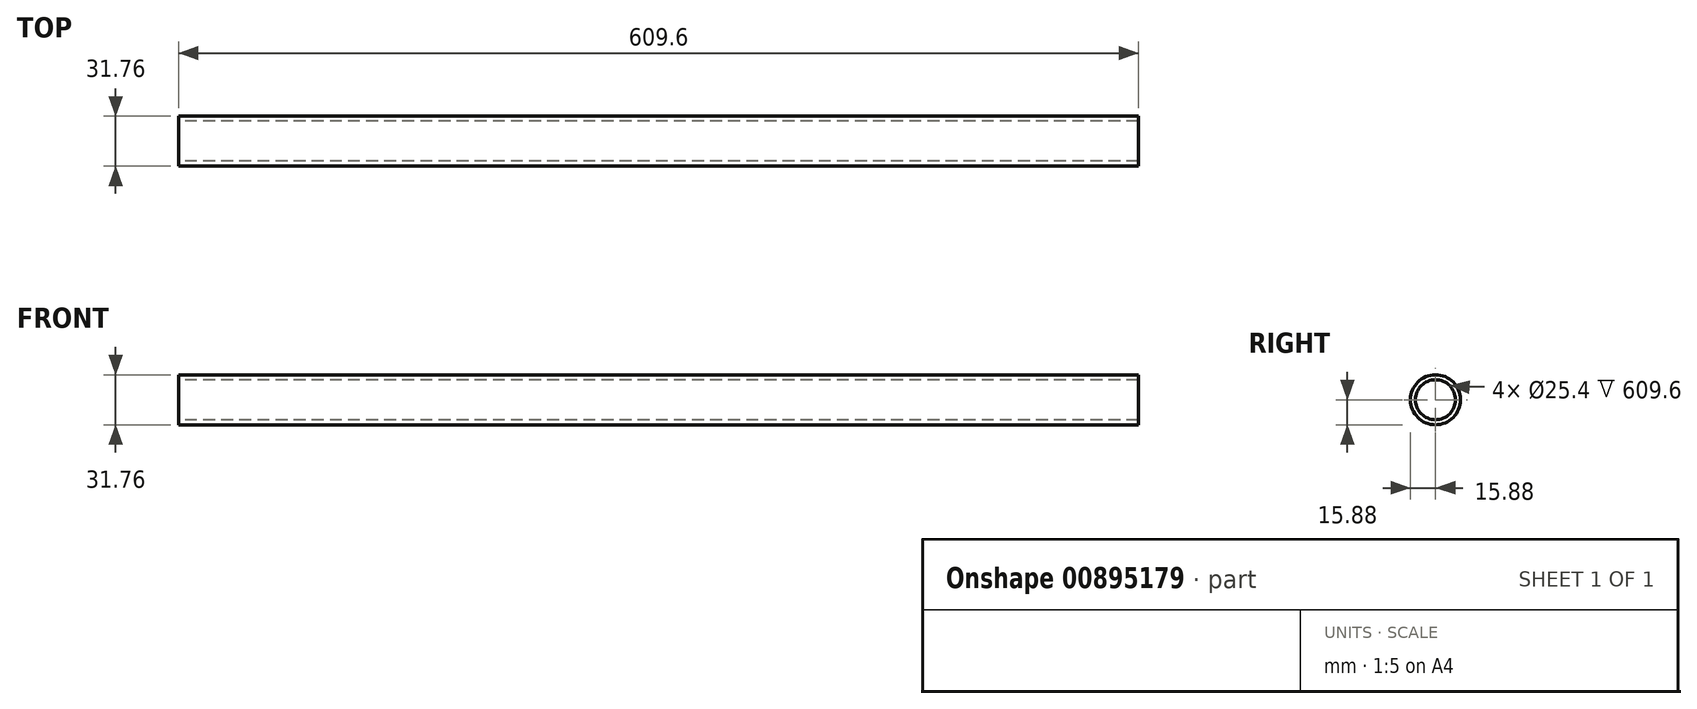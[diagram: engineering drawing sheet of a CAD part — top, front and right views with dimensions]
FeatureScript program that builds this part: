
annotation { "Feature Type Name" : "Feature", "Feature Type Description" : "" }
export const myFeature = defineFeature(function(context is Context, id is Id, definition is map)
    precondition{}
    {
        {
            var Q0;
            Q0=qCreatedBy(makeId("Right.planeOp"),FACE);
            var sketch = newSketch(context, id + "F0", { "sketchPlane" : qUnion([Q0])});
            skCircle(sketch, "E0", {"center": v(0, 0) * mm, "radius": 12.7 * mm});
            skCircle(sketch, "E1", {"center": v(0, 0) * mm, "radius": 15.88 * mm});
            skSolve(sketch);
        }
        {
            var Q0;
            Q0=qSketchRegion(id+"F0",true);
            extrude(context, id + "F1", {"entities" : qUnion([Q0]), "depth" : 609.6 * mm, "offsetDistance" : 25 * mm});
        }
    });
